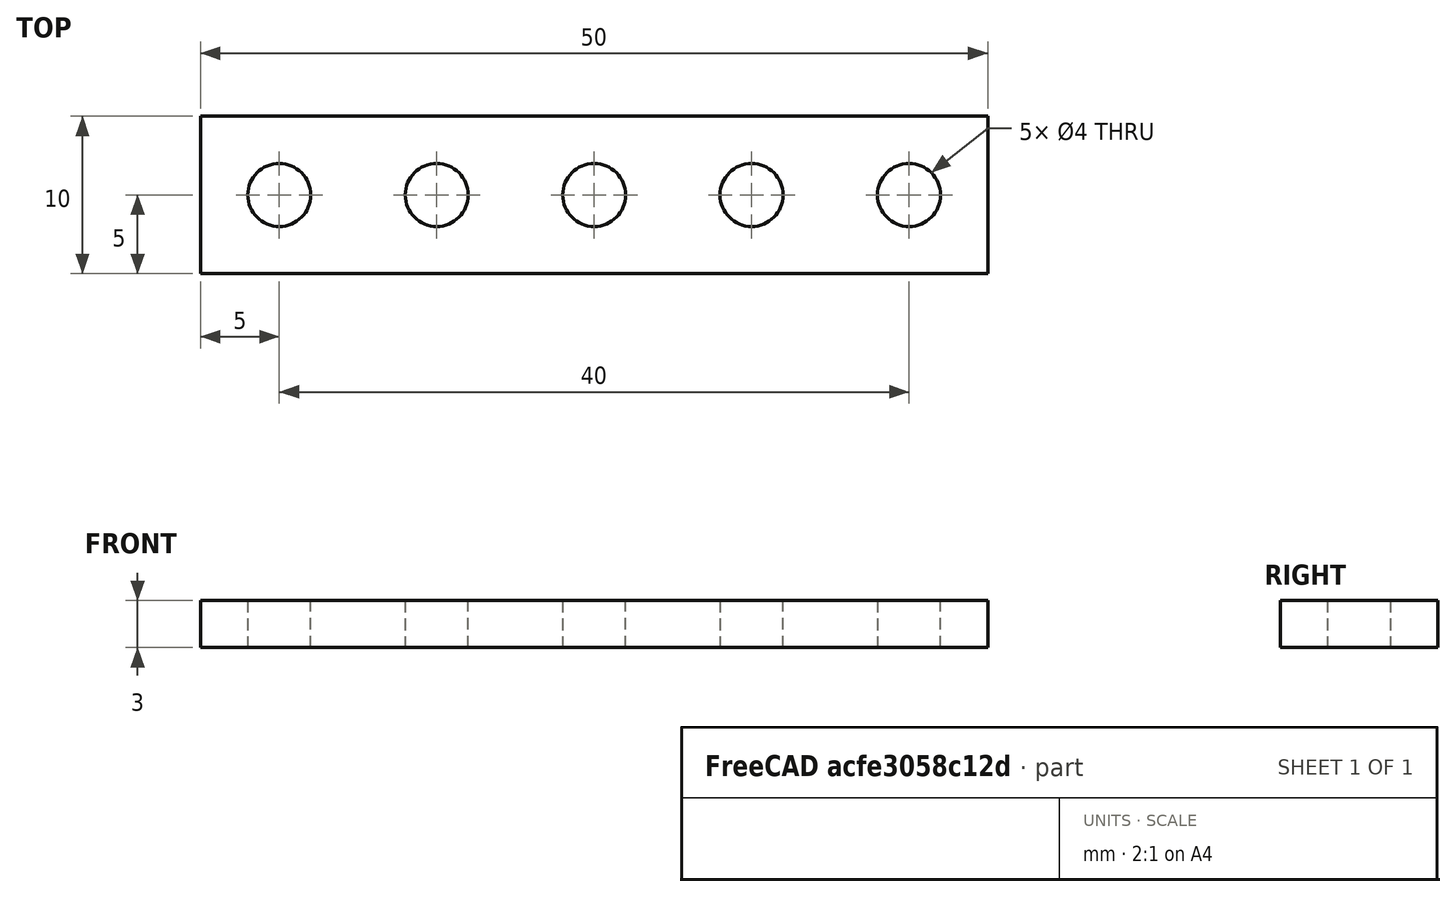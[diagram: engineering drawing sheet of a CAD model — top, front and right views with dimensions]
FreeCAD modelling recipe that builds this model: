
FCSTD DOCUMENT  (FreeCAD 0.17R13217 (Git))
Label: 10-pieza-mecano-5
License: All rights reserved
LicenseURL: http://en.wikipedia.org/wiki/All_rights_reserved
objects: Sketcher::SketchObject×1, PartDesign::Pad×1, PartDesign::Body×1
note: 4 computed .brp shape members not serialized (recipe doc carries the construction recipe); baked Part::Feature solids carry a one-line shape summary decoded from their .brp

FEATURE [Sketcher::SketchObject] Sketch
  MapMode = 5
  Support = -> [XY_Plane]
  sketch-geometry (11):
    g0: LineSegment StartX=-25 StartY=5 StartZ=0 EndX=25 EndY=5 EndZ=0
    g1: LineSegment StartX=25 StartY=5 StartZ=0 EndX=25 EndY=-5 EndZ=0
    g2: LineSegment StartX=25 StartY=-5 StartZ=0 EndX=-25 EndY=-5 EndZ=0
    g3: LineSegment StartX=-25 StartY=-5 StartZ=0 EndX=-25 EndY=5 EndZ=0
    g4: Circle CenterX=0 CenterY=0 CenterZ=0 NormalX=0 NormalY=0 NormalZ=1 AngleXU=0 Radius=2
    g5: Circle CenterX=-10 CenterY=0 CenterZ=0 NormalX=0 NormalY=0 NormalZ=1 AngleXU=0 Radius=2
    g6: Circle CenterX=-20 CenterY=0 CenterZ=0 NormalX=0 NormalY=0 NormalZ=1 AngleXU=0 Radius=2
    g7: Circle CenterX=10 CenterY=0 CenterZ=0 NormalX=0 NormalY=0 NormalZ=1 AngleXU=0 Radius=2
    g8: Circle CenterX=20 CenterY=0 CenterZ=0 NormalX=0 NormalY=0 NormalZ=1 AngleXU=0 Radius=2
    g9: LineSegment [constr] StartX=-20 StartY=0 StartZ=0 EndX=-10 EndY=0 EndZ=0
    g10: LineSegment [constr] StartX=-10 StartY=0 StartZ=0 EndX=0 EndY=0 EndZ=0
  constraints (31):
    c: Coincident(g0,g1)
    c: Coincident(g1,g2)
    c: Coincident(g2,g3)
    c: Coincident(g3,g0)
    c: Horizontal(g0)
    c: Horizontal(g2)
    c: Vertical(g1)
    c: Vertical(g3)
    c: DistanceY(g3,g3) = 10
    c: Symmetric(g0,g1,g-1)
    c: Coincident(g4,g-1)
    c: Radius(g4) = 2
    c: PointOnObject(g5,g-1)
    c: PointOnObject(g6,g-1)
    c: PointOnObject(g7,g-1)
    c: PointOnObject(g8,g-1)
    c: Symmetric(g6,g8,g-2)
    c: Symmetric(g5,g7,g-2)
    c: Equal(g6,g5)
    c: Equal(g5,g4)
    c: Equal(g4,g7)
    c: Equal(g7,g8)
    c: DistanceX(g5,g-1) = 10
    c: Coincident(g9,g6)
    c: Coincident(g9,g5)
    c: Horizontal(g9)
    c: Coincident(g10,g5)
    c: Coincident(g10,g-1)
    c: Horizontal(g10)
    c: Equal(g9,g10)
    c: DistanceX(g0,g6) = 5
FEATURE [PartDesign::Pad] Pad
  Length = 3
  Length2 = 100
  Profile = -> Sketch
  Refine = true
  Type = 0
FEATURE [PartDesign::Body] Body
  Group = -> [Sketch,Pad]
  Origin = -> Origin
  Tip = -> Pad
